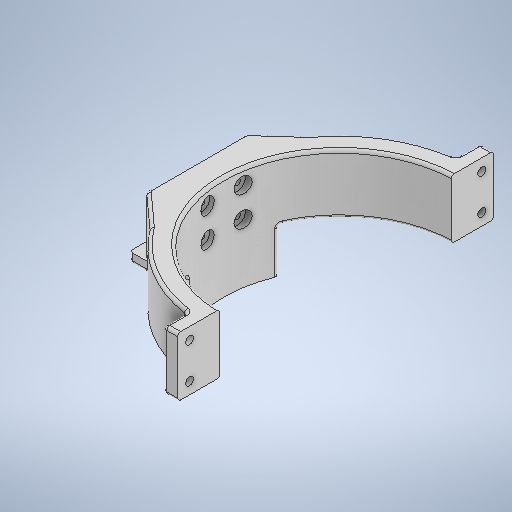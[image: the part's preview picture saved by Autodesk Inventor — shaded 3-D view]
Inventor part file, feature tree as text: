
AUTODESK INVENTOR PART (.ipt)
format: ipt  version: 2025.1 (Build 291241000, 241)  size: 632,320 bytes
history: native  units: mm
features: extrude x10, sketch x9, fillet x3, other x2
ambient origin geometry x8: Origin, YZ Plane, XZ Plane, XY Plane, X Axis, Y Axis, Z Axis, Center Point
bodies: Solide1 (feature_tree)
feature tree (24):
  extrude  "Extrusion1"  Depth=137.383mm
  fillet  "Congé2"  Radius=117.383mm
  fillet  "Congé3"  Radius=2.0mm
  extrude  "Extrusion2"  Depth=7.0mm
  extrude  "Extrusion3"  Depth=160.0mm
  extrude  "Extrusion4"  Depth=25.887mm
  other  "Plan de construction1"
  extrude  "Extrusion5"  Depth=14.0mm
  extrude  "Extrusion6"  Depth=1.0mm
  extrude  "Extrusion7"  Depth=30.0mm TaperAngle=0.0deg
  extrude  "Extrusion8"  Depth=2.0mm
  extrude  "Extrusion9"  Depth=3.0mm
  extrude  "Extrusion10"  Depth=6.0mm
  fillet  "Congé5"  Radius=6.0mm
  sketch  "Esquisse1"
  sketch  "Esquisse2"
  sketch  "Esquisse3"
  other  "Réseau d'esquisse circulaire1"
  sketch  "Esquisse4"
  sketch  "Esquisse6"
  sketch  "Esquisse7"
  sketch  "Esquisse5"
  sketch  "Esquisse9"
  sketch  "Esquisse11"
